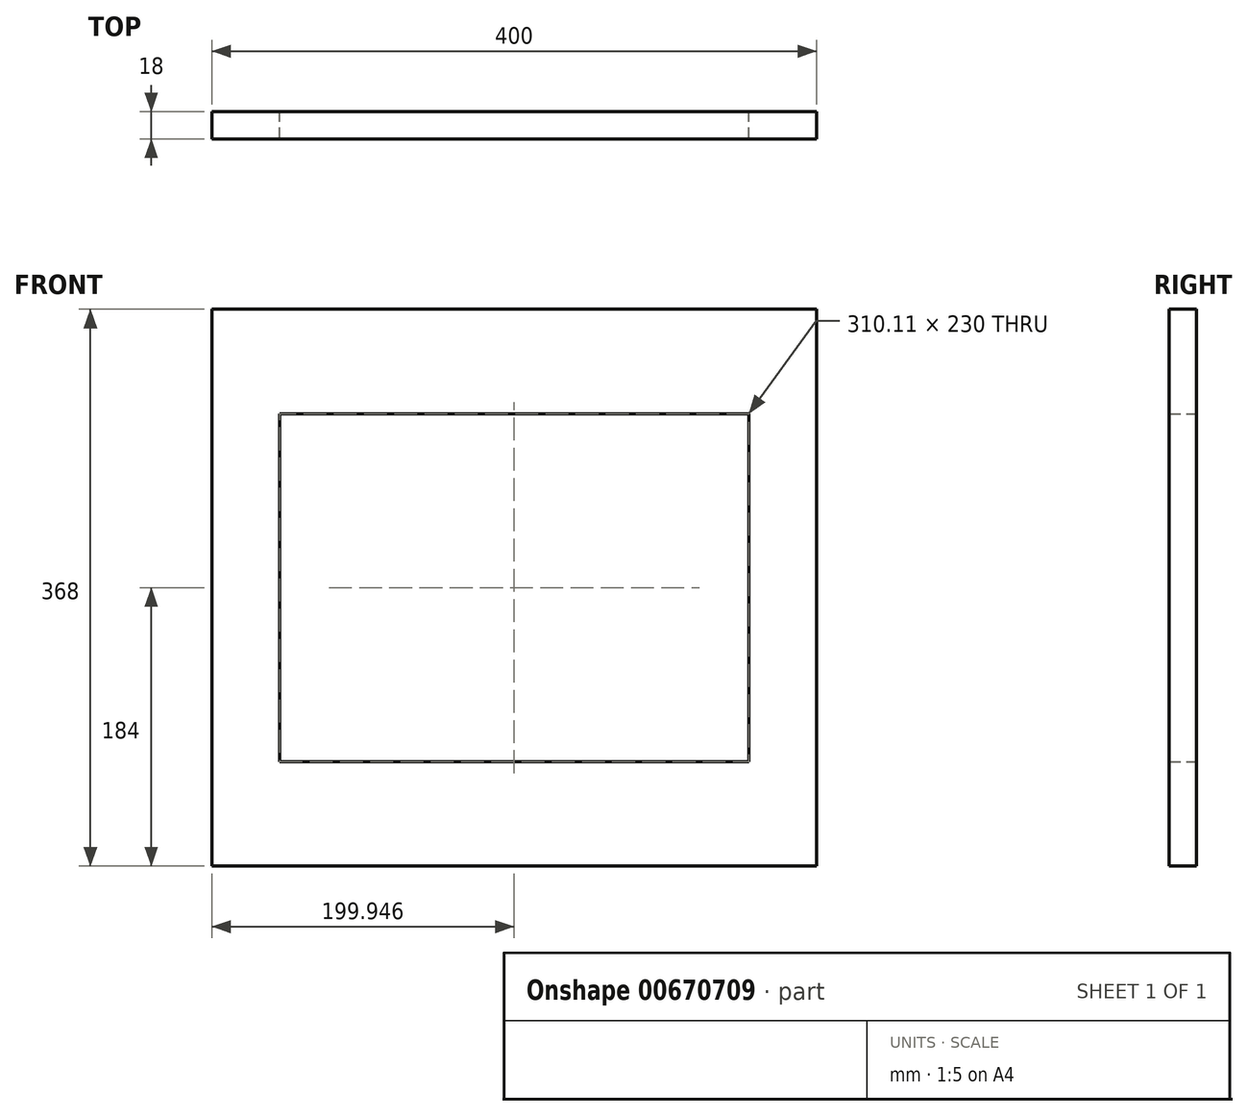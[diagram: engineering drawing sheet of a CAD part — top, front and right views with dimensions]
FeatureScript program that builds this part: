
annotation { "Feature Type Name" : "Feature", "Feature Type Description" : "" }
export const myFeature = defineFeature(function(context is Context, id is Id, definition is map)
    precondition{}
    {
        {
            var Q0;
            Q0=qCreatedBy(makeId("Front.planeOp"),FACE);
            var sketch = newSketch(context, id + "F0", { "sketchPlane" : qUnion([Q0])});
            skLineSegment(sketch, "E0.bottom", {"start": v(0, 0) * mm, "end": v(-400, 0) * mm});
            skLineSegment(sketch, "E0.top", {"start": v(0, 368) * mm, "end": v(-400, 368) * mm});
            skLineSegment(sketch, "E0.left", {"start": v(0, 0) * mm, "end": v(0, 368) * mm});
            skLineSegment(sketch, "E0.right", {"start": v(-400, 0) * mm, "end": v(-400, 368) * mm});
            skLineSegment(sketch, "E1.bottom", {"start": v(-400, 368) * mm, "end": v(-355.1, 368) * mm});
            skLineSegment(sketch, "E1.top", {"start": v(-400, 0) * mm, "end": v(-355.1, 0) * mm});
            skLineSegment(sketch, "E1.left", {"start": v(-400, 368) * mm, "end": v(-400, 0) * mm});
            skLineSegment(sketch, "E1.right", {"start": v(-355.1, 368) * mm, "end": v(-355.1, 0) * mm});
            skLineSegment(sketch, "E2.bottom", {"start": v(0, 368) * mm, "end": v(-45, 368) * mm});
            skLineSegment(sketch, "E2.top", {"start": v(0, 0) * mm, "end": v(-45, 0) * mm});
            skLineSegment(sketch, "E2.left", {"start": v(0, 368) * mm, "end": v(0, 0) * mm});
            skLineSegment(sketch, "E2.right", {"start": v(-45, 368) * mm, "end": v(-45, 0) * mm});
            skLineSegment(sketch, "E3.bottom", {"start": v(-355.1, 368) * mm, "end": v(-45, 368) * mm});
            skLineSegment(sketch, "E3.top", {"start": v(-355.1, 299) * mm, "end": v(-45, 299) * mm});
            skLineSegment(sketch, "E3.left", {"start": v(-355.1, 368) * mm, "end": v(-355.1, 299) * mm});
            skLineSegment(sketch, "E3.right", {"start": v(-45, 368) * mm, "end": v(-45, 299) * mm});
            skLineSegment(sketch, "E4.bottom", {"start": v(-355.1, 0) * mm, "end": v(-45, 0) * mm});
            skLineSegment(sketch, "E4.top", {"start": v(-355.1, 69) * mm, "end": v(-45, 69) * mm});
            skLineSegment(sketch, "E4.left", {"start": v(-355.1, 0) * mm, "end": v(-355.1, 69) * mm});
            skLineSegment(sketch, "E4.right", {"start": v(-45, 0) * mm, "end": v(-45, 69) * mm});
            skSolve(sketch);
        }
        {
            var Q0;
            Q0 = qSketchRegion(id + "F0", true);
            extrude(context, id + "F1", {"entities" : qUnion([Q0]), "depth" : 18 * mm, "offsetDistance" : 25 * mm});
        }
    });
